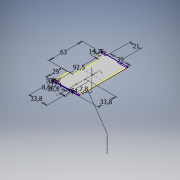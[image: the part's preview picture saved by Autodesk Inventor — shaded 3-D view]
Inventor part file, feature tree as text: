
AUTODESK INVENTOR PART (.ipt)
format: ipt  version: 2019 (Build 230136000, 136)  size: 163,328 bytes
history: native  units: mm
features: other x7, extrude x2, sketch x1
ambient origin geometry x8: Origin, YZ Plane, XZ Plane, XY Plane, X Axis, Y Axis, Z Axis, Center Point
bodies: Body1 (feature_tree)
feature tree (10):
  other  "Bryła1"
  other  "Opisy"
  sketch  "Szkic1"
  extrude  "Plytka"  Depth=39.0mm
  extrude  "Otwory"  Depth=92.5mm
  other  "Marginesy(Nie dotycza spodu plytki w strefie czujnika lini)"
  other  "Tekst linii odniesienia 1"
  other  "Tekst linii odniesienia 2"
  other  "Tekst linii odniesienia 3"
  other  "Tekst linii odniesienia 4"
